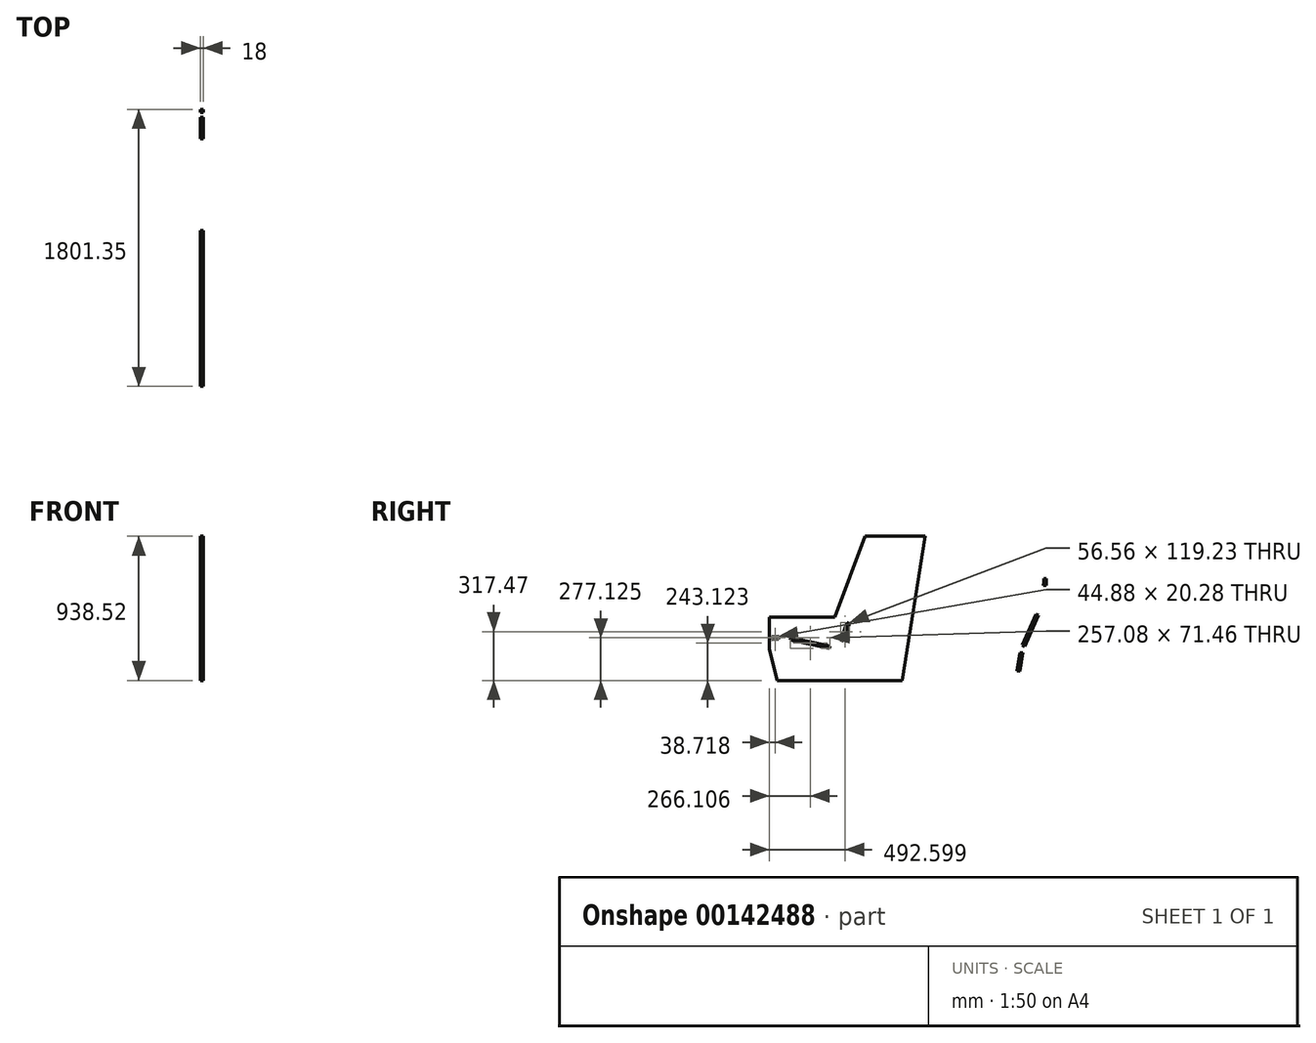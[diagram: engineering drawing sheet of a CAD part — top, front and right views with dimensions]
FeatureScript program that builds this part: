
annotation { "Feature Type Name" : "Feature", "Feature Type Description" : "" }
export const myFeature = defineFeature(function(context is Context, id is Id, definition is map)
    precondition{}
    {
        {
            var Q0;
            Q0=qCreatedBy(makeId("Right.planeOp"),FACE);
            var sketch = newSketch(context, id + "F0", { "sketchPlane" : qUnion([Q0])});
            skLineSegment(sketch, "E0", {"start": v(863.87, 92.47) * mm, "end": v(1011.61, 1031) * mm});
            skLineSegment(sketch, "E1", {"start": v(1011.61, 1031) * mm, "end": v(622.16, 1031) * mm});
            skLineSegment(sketch, "E2", {"start": v(622.16, 1031) * mm, "end": v(427.2, 503.9) * mm});
            skLineSegment(sketch, "E3", {"start": v(427.2, 503.9) * mm, "end": v(0, 503.9) * mm});
            skLineSegment(sketch, "E4", {"start": v(0, 503.9) * mm, "end": v(0, 298.18) * mm});
            skLineSegment(sketch, "E5", {"start": v(394.65, 317.47) * mm, "end": v(141.3, 371.32) * mm});
            skLineSegment(sketch, "E6", {"start": v(60.22, 379.73) * mm, "end": v(16.28, 377.43) * mm});
            skLineSegment(sketch, "E7.0", {"start": v(390.9, 299.86) * mm, "end": v(137.57, 353.71) * mm});
            skLineSegment(sketch, "E8.0", {"start": v(61.16, 361.76) * mm, "end": v(17.22, 359.46) * mm});
            skLineSegment(sketch, "E9", {"start": v(394.65, 317.47) * mm, "end": v(390.9, 299.86) * mm});
            skLineSegment(sketch, "E10", {"start": v(141.3, 371.32) * mm, "end": v(137.57, 353.71) * mm});
            skLineSegment(sketch, "E11", {"start": v(60.22, 379.73) * mm, "end": v(61.16, 361.76) * mm});
            skLineSegment(sketch, "E12", {"start": v(16.28, 377.43) * mm, "end": v(17.22, 359.46) * mm});
            skLineSegment(sketch, "E13", {"start": v(503.88, 469.55) * mm, "end": v(464.32, 356.26) * mm});
            skPoint(sketch, "E14.visualSharp", {"position": v(446.9, 306.37) * mm});
            skLineSegment(sketch, "E15", {"start": v(464.32, 356.26) * mm, "end": v(481.31, 350.33) * mm});
            skLineSegment(sketch, "E16.0", {"start": v(520.88, 463.62) * mm, "end": v(481.31, 350.33) * mm});
            skLineSegment(sketch, "E17.0", {"start": v(503.88, 469.55) * mm, "end": v(520.88, 463.62) * mm});
            skLineSegment(sketch, "E18", {"start": v(863.87, 92.47) * mm, "end": v(50.68, 92.47) * mm});
            skPoint(sketch, "E19.end.orphan", {"position": v(849.31, 0) * mm});
            skLineSegment(sketch, "E20", {"start": v(0, 298.18) * mm, "end": v(50.68, 92.47) * mm});
            skPoint(sketch, "E21.orphan", {"position": v(0, 92.47) * mm});
            skLineSegment(sketch, "E22.0.0", {"start": v(1629.69, 274.2) * mm, "end": v(1610.91, 155.67) * mm});
            skLineSegment(sketch, "E22.0.1", {"start": v(1610.91, 155.67) * mm, "end": v(1628.7, 152.85) * mm});
            skLineSegment(sketch, "E22.0.2", {"start": v(1628.7, 152.85) * mm, "end": v(1647.46, 271.37) * mm});
            skLineSegment(sketch, "E22.0.3", {"start": v(1647.46, 271.37) * mm, "end": v(1629.69, 274.2) * mm});
            skArc(sketch, "E22.2.0", {"start": v(1783.35, 735.6) * mm, "mid": v(1783.2, 723.64) * mm, "end": v(1782.76, 711.67) * mm});
            skLineSegment(sketch, "E22.2.1", {"start": v(1782.76, 711.67) * mm, "end": v(1800.78, 711.67) * mm});
            skArc(sketch, "E22.2.2", {"start": v(1800.78, 711.67) * mm, "mid": v(1801.2, 723.64) * mm, "end": v(1801.35, 735.6) * mm});
            skLineSegment(sketch, "E22.2.3", {"start": v(1801.35, 735.6) * mm, "end": v(1801.35, 754.6) * mm});
            skLineSegment(sketch, "E22.2.4", {"start": v(1801.35, 754.6) * mm, "end": v(1783.35, 754.6) * mm});
            skLineSegment(sketch, "E22.2.5", {"start": v(1783.35, 754.6) * mm, "end": v(1783.35, 735.6) * mm});
            skLineSegment(sketch, "E23.0", {"start": v(1645, 322.82) * mm, "end": v(1661.44, 315.5) * mm});
            skLineSegment(sketch, "E23.1", {"start": v(1661.44, 315.5) * mm, "end": v(1750.92, 516.48) * mm});
            skLineSegment(sketch, "E23.2", {"start": v(1750.92, 516.48) * mm, "end": v(1734.47, 523.8) * mm});
            skLineSegment(sketch, "E23.3", {"start": v(1645, 322.82) * mm, "end": v(1734.47, 523.8) * mm});
            skSolve(sketch);
        }
        {
            var Q0;
            Q0 = qSketchRegion(id + "F0", true);
            extrude(context, id + "F1", {"entities" : qUnion([Q0]), "depth" : 18 * mm});
        }
    });
